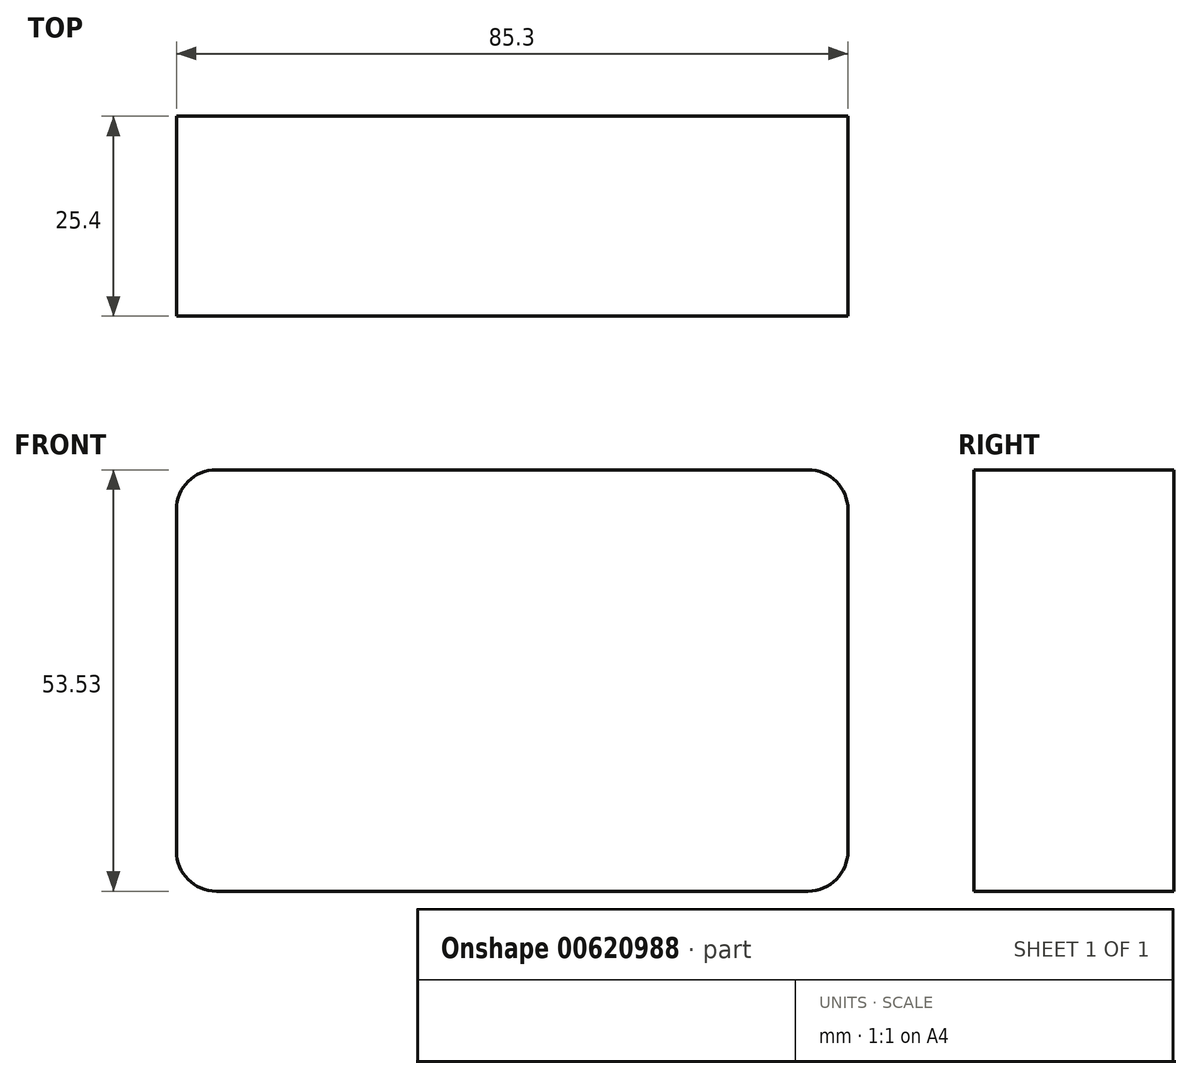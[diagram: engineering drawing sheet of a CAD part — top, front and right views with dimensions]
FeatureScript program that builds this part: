
annotation { "Feature Type Name" : "Feature", "Feature Type Description" : "" }
export const myFeature = defineFeature(function(context is Context, id is Id, definition is map)
    precondition{}
    {
        {
            var Q0;
            Q0=qCreatedBy(makeId("Front.planeOp"),FACE);
            var sketch = newSketch(context, id + "F0", { "sketchPlane" : qUnion([Q0])});
            skLineSegment(sketch, "E0.bottom", {"start": v(-54.46, -19.42) * mm, "end": v(30.84, -19.42) * mm});
            skLineSegment(sketch, "E0.top", {"start": v(-54.46, 34.1) * mm, "end": v(30.84, 34.1) * mm});
            skLineSegment(sketch, "E0.left", {"start": v(-54.46, -19.42) * mm, "end": v(-54.46, 34.1) * mm});
            skLineSegment(sketch, "E0.right", {"start": v(30.84, -19.42) * mm, "end": v(30.84, 34.1) * mm});
            skSolve(sketch);
        }
        {
            var Q0;
            Q0=makeQuery(id+"F0.imprint","IMPRINT",FACE,{"disambiguationData":[TD([[makeQuery(id+"F0.imprint","IMPRINT",EDGE,{"derivedFrom":sQuery(id+"F0.wireOp",EDGE,"E0.bottom")}),1.0]])]});
            extrude(context, id + "F1", {"entities" : qUnion([Q0]), "oppositeDirection" : true, "depth" : 25.4 * mm, "offsetDistance" : 25.4 * mm});
        }
        {
            var Q0;
            Q0=makeQuery(id+"F1.opExtrude","SWEPT_EDGE",EDGE,{"disambiguationData":[OSD([sQuery(id+"F0.wireOp",EDGE,"E0.top"),sQuery(id+"F0.wireOp",EDGE,"E0.right")])]});
            var Q1;
            Q1=makeQuery(id+"F1.opExtrude","SWEPT_EDGE",EDGE,{"disambiguationData":[OSD([sQuery(id+"F0.wireOp",EDGE,"E0.bottom"),sQuery(id+"F0.wireOp",EDGE,"E0.right")])]});
            fillet(context, id + "F2", {"entities" : qUnion([Q0, Q1]), "radius" : 5.08 * mm, "tangentPropagation" : true, "allowEdgeOverflow" : false});
        }
        {
            var Q0;
            Q0=makeQuery(id+"F1.opExtrude","SWEPT_EDGE",EDGE,{"disambiguationData":[OSD([sQuery(id+"F0.wireOp",EDGE,"E0.top"),sQuery(id+"F0.wireOp",EDGE,"E0.left")])]});
            var Q1;
            Q1=makeQuery(id+"F1.opExtrude","SWEPT_EDGE",EDGE,{"disambiguationData":[OSD([sQuery(id+"F0.wireOp",EDGE,"E0.bottom"),sQuery(id+"F0.wireOp",EDGE,"E0.left")])]});
            fillet(context, id + "F3", {"entities" : qUnion([Q0, Q1]), "radius" : 5.08 * mm, "tangentPropagation" : true, "allowEdgeOverflow" : false});
        }
        {
            var Q0;
            Q0=qCreatedBy(makeId("Top.planeOp"),FACE);
            var sketch = newSketch(context, id + "F4", { "sketchPlane" : qUnion([Q0])});
            skLineSegment(sketch, "E1", {"start": v(-53.85, -45.67) * mm, "end": v(-3.05, -45.67) * mm});
            skLineSegment(sketch, "E2.bottom", {"start": v(-61.76, -55.62) * mm, "end": v(-112.56, -55.62) * mm});
            skLineSegment(sketch, "E2.top", {"start": v(-61.76, -4.82) * mm, "end": v(-112.56, -4.82) * mm});
            skLineSegment(sketch, "E2.left", {"start": v(-61.76, -55.62) * mm, "end": v(-61.76, -4.82) * mm});
            skLineSegment(sketch, "E2.right", {"start": v(-112.56, -55.62) * mm, "end": v(-112.56, -4.82) * mm});
            skSolve(sketch);
        }
        {
            var Q0;
            Q0=makeQuery(id+"F4.imprint","IMPRINT",FACE,{"disambiguationData":[TD([[makeQuery(id+"F4.imprint","IMPRINT",EDGE,{"derivedFrom":sQuery(id+"F4.wireOp",EDGE,"E2.bottom")}),-1.0]])]});
            var Q1;
            Q1=sQuery(id+"F4.wireOp",EDGE,"E2.left");
            revolve(context, id + "F5", {"entities" : qUnion([Q0]), "axis" : qUnion([Q1]), "revolveType" : RevolveType.SYMMETRIC, "angle" : 30 * degree});
        }
        {
            var Q0;
            Q0=makeQuery(id+"F5.opRevolve","SWEPT_BODY",BODY,{"disambiguationData":[OSD([sQuery(id+"F4.wireOp",EDGE,"E2.bottom"),sQuery(id+"F4.wireOp",EDGE,"E2.top"),sQuery(id+"F4.wireOp",EDGE,"E2.left"),sQuery(id+"F4.wireOp",EDGE,"E2.right")])]});
            deleteBodies(context, id + "F6", {"entities" : qUnion([Q0])});
        }
    });
